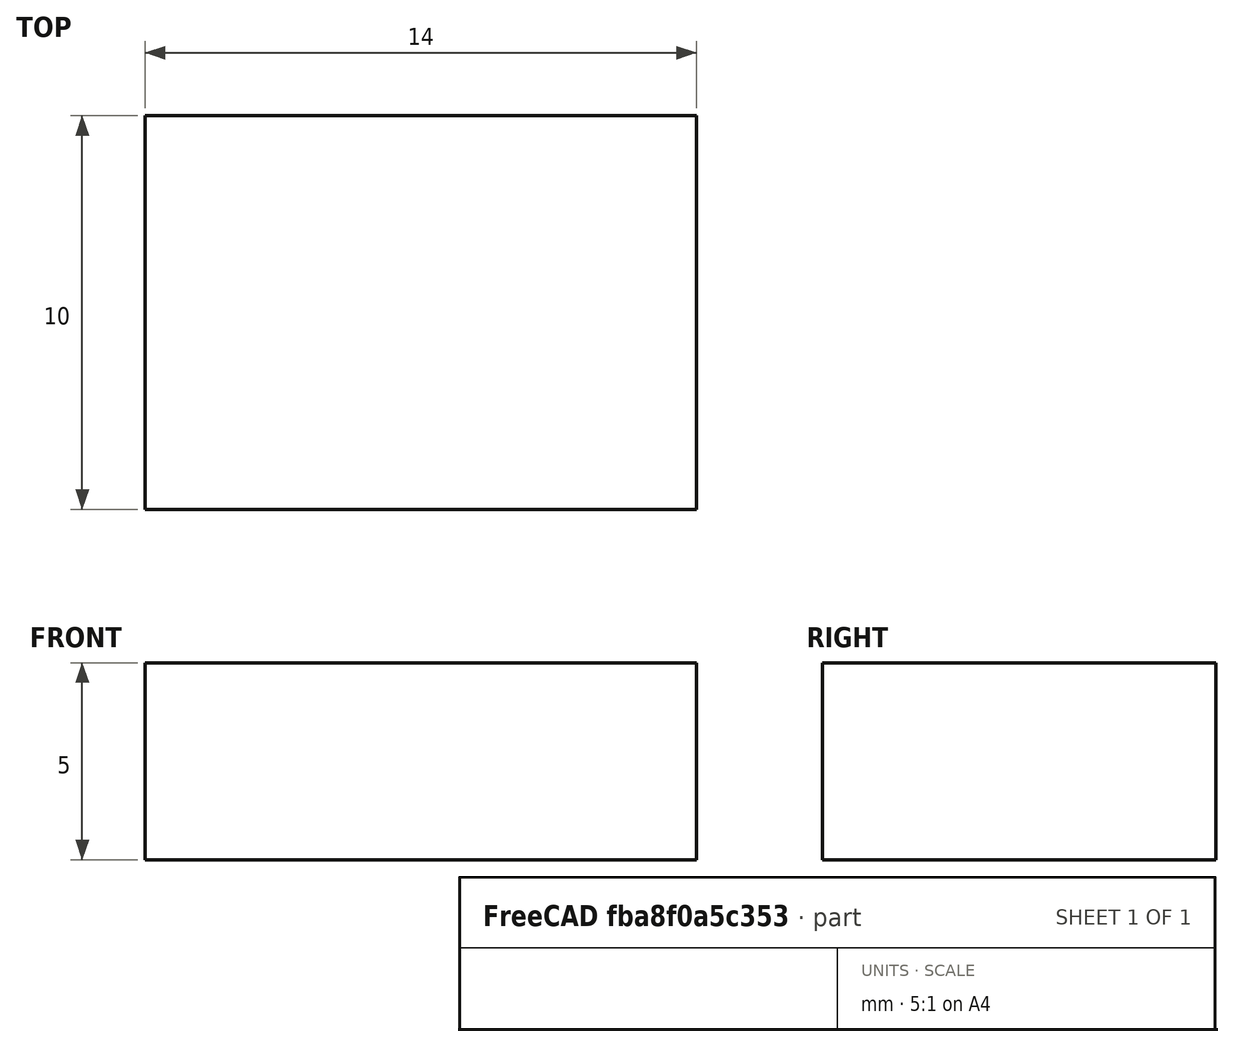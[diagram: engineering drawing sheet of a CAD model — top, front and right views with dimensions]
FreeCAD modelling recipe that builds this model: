
FCSTD DOCUMENT  (FreeCAD 0.19R24291 (Git))
Label: CenteredRectangleParameterized
License: All rights reserved
LicenseURL: http://en.wikipedia.org/wiki/All_rights_reserved
objects: Sketcher::SketchObject×1, Spreadsheet::Sheet×1, PartDesign::Pad×1, PartDesign::Body×1
note: 4 computed .brp shape members not serialized (recipe doc carries the construction recipe); baked Part::Feature solids carry a one-line shape summary decoded from their .brp

FEATURE [Sketcher::SketchObject] Sketch
  FullyConstrained = true
  MapMode = 5
  Support = -> [XY_Plane]
  expr: Constraints[11] = <<SpreadsheetRectangleOffset>>.Width
  expr: Constraints[12] = <<SpreadsheetRectangleOffset>>.Height
  expr: Constraints[1] = <<SpreadsheetRectangleOffset>>.OffsetVert
  expr: Constraints[0] = <<SpreadsheetRectangleOffset>>.OffsetHorz
  sketch-geometry (5):
    g0: GeomPoint X=5 Y=6 Z=0
    g1: LineSegment StartX=-2 StartY=11 StartZ=0 EndX=12 EndY=11 EndZ=0
    g2: LineSegment StartX=12 StartY=11 StartZ=0 EndX=12 EndY=1 EndZ=0
    g3: LineSegment StartX=12 StartY=1 StartZ=0 EndX=-2 EndY=1 EndZ=0
    g4: LineSegment StartX=-2 StartY=1 StartZ=0 EndX=-2 EndY=11 EndZ=0
  constraints (13):
    c: DistanceX(g-1,g0) = 5
    c: DistanceY(g-1,g0) = 6
    c: Coincident(g1,g2)
    c: Coincident(g2,g3)
    c: Coincident(g3,g4)
    c: Coincident(g4,g1)
    c: Horizontal(g1)
    c: Horizontal(g3)
    c: Vertical(g2)
    c: Vertical(g4)
    c: Symmetric(g1,g2,g0)
    c: DistanceX(g1,g1) = 14
    c: DistanceY(g2,g2) = 10
FEATURE [Spreadsheet::Sheet] Spreadsheet  label="SpreadsheetRectangleOffset"
  cells = A1=Centered Rectangle; A2=Place a center point. Locate that point at Horz and Vertical Offset; A3=Place a rectangle around the point. ; A4=Select upper left corner, lower right cornder and center point. Set symetery; A5=Set Width to Width parameter (below), Set Height to Height Parameter below.; A6=Close the now fully parameterized and constrinaed sketch.; A7=Pad the sketch to the Depth prameter (below).; A9=OffsetHorz; B9(OffsetHorz)==5mm; A10=OffsetVert; B10(OffsetVert)==6mm; A12=Width; B12(Width)==14mm; A13=Height; B13(Height)==10mm; A14=Depth; B14(Depth)==5mm
FEATURE [PartDesign::Pad] Pad
  Direction = (1,1,1)
  Length = 5
  Length2 = 100
  Profile = -> Sketch
  Type = 0
  expr: Length = <<SpreadsheetRectangleOffset>>.Depth
FEATURE [PartDesign::Body] Body
  Group = -> [Sketch,Pad]
  Origin = -> Origin
  Tip = -> Pad
